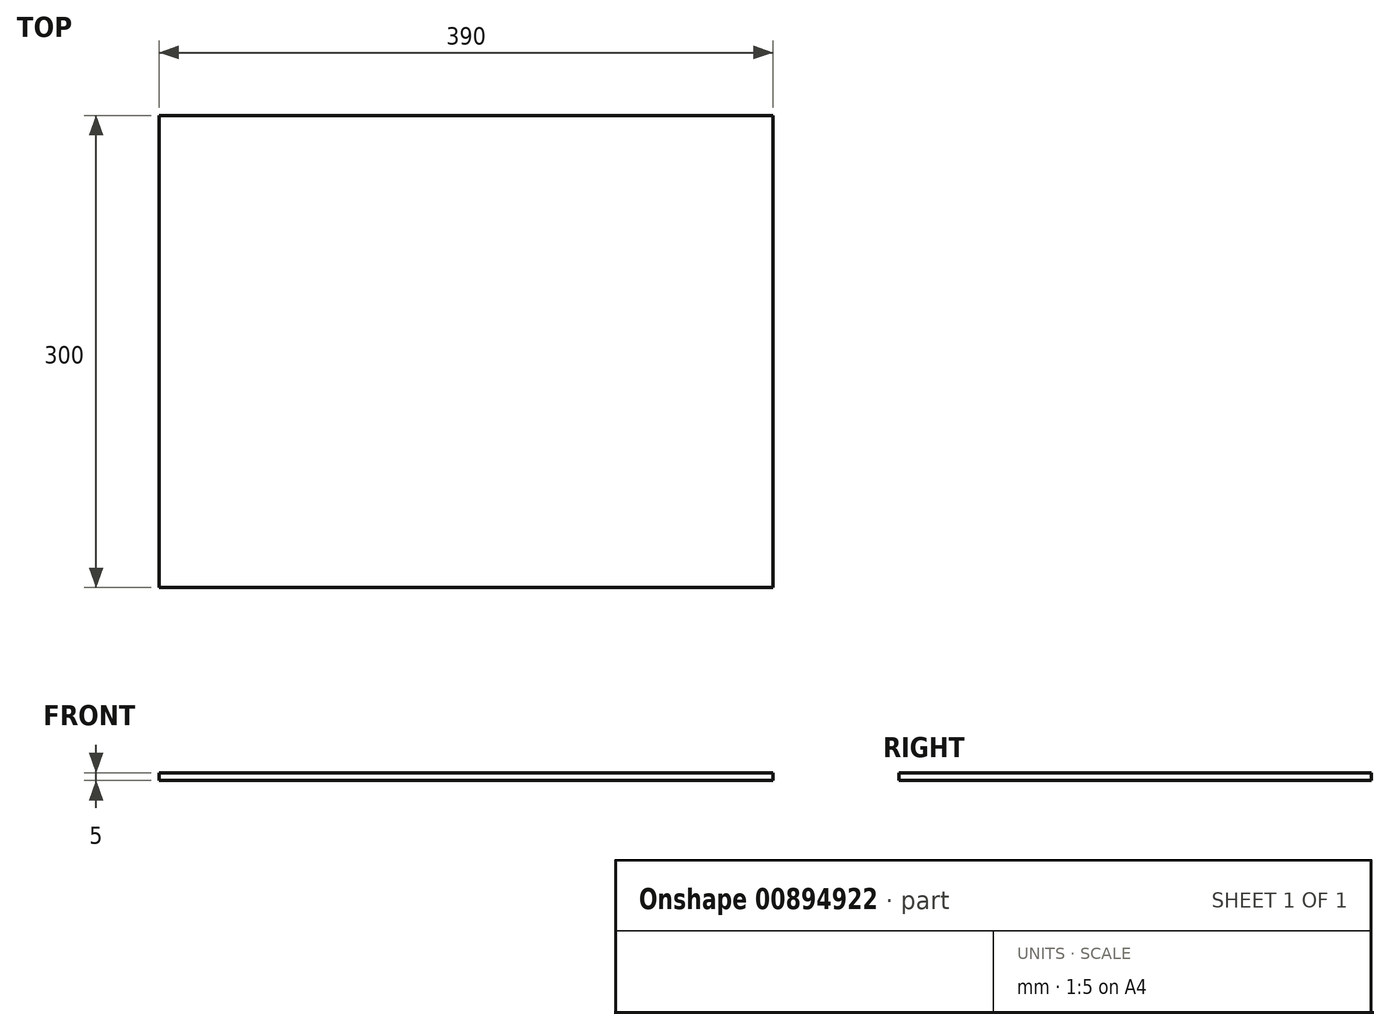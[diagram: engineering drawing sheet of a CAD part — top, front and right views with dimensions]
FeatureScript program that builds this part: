
annotation { "Feature Type Name" : "Feature", "Feature Type Description" : "" }
export const myFeature = defineFeature(function(context is Context, id is Id, definition is map)
    precondition{}
    {
        {
            var Q0;
            Q0=qCreatedBy(makeId("Top.planeOp"),FACE);
            var sketch = newSketch(context, id + "F0", { "sketchPlane" : qUnion([Q0])});
            skLineSegment(sketch, "E0.bottom", {"start": v(-195, 150) * mm, "end": v(195, 150) * mm});
            skLineSegment(sketch, "E0.top", {"start": v(-195, -150) * mm, "end": v(195, -150) * mm});
            skLineSegment(sketch, "E0.left", {"start": v(-195, 150) * mm, "end": v(-195, -150) * mm});
            skLineSegment(sketch, "E0.right", {"start": v(195, 150) * mm, "end": v(195, -150) * mm});
            skPoint(sketch, "E0.middle", {"position": v(0, 0) * mm});
            skSolve(sketch);
        }
        {
            var Q0;
            Q0=makeQuery(id+"F0.imprint","IMPRINT",FACE,{"disambiguationData":[TD([[makeQuery(id+"F0.imprint","IMPRINT",EDGE,{"derivedFrom":sQuery(id+"F0.wireOp",EDGE,"E0.bottom")}),-1.0]])]});
            extrude(context, id + "F1", {"entities" : qUnion([Q0]), "depth" : 5 * mm, "offsetDistance" : 25 * mm});
        }
    });
